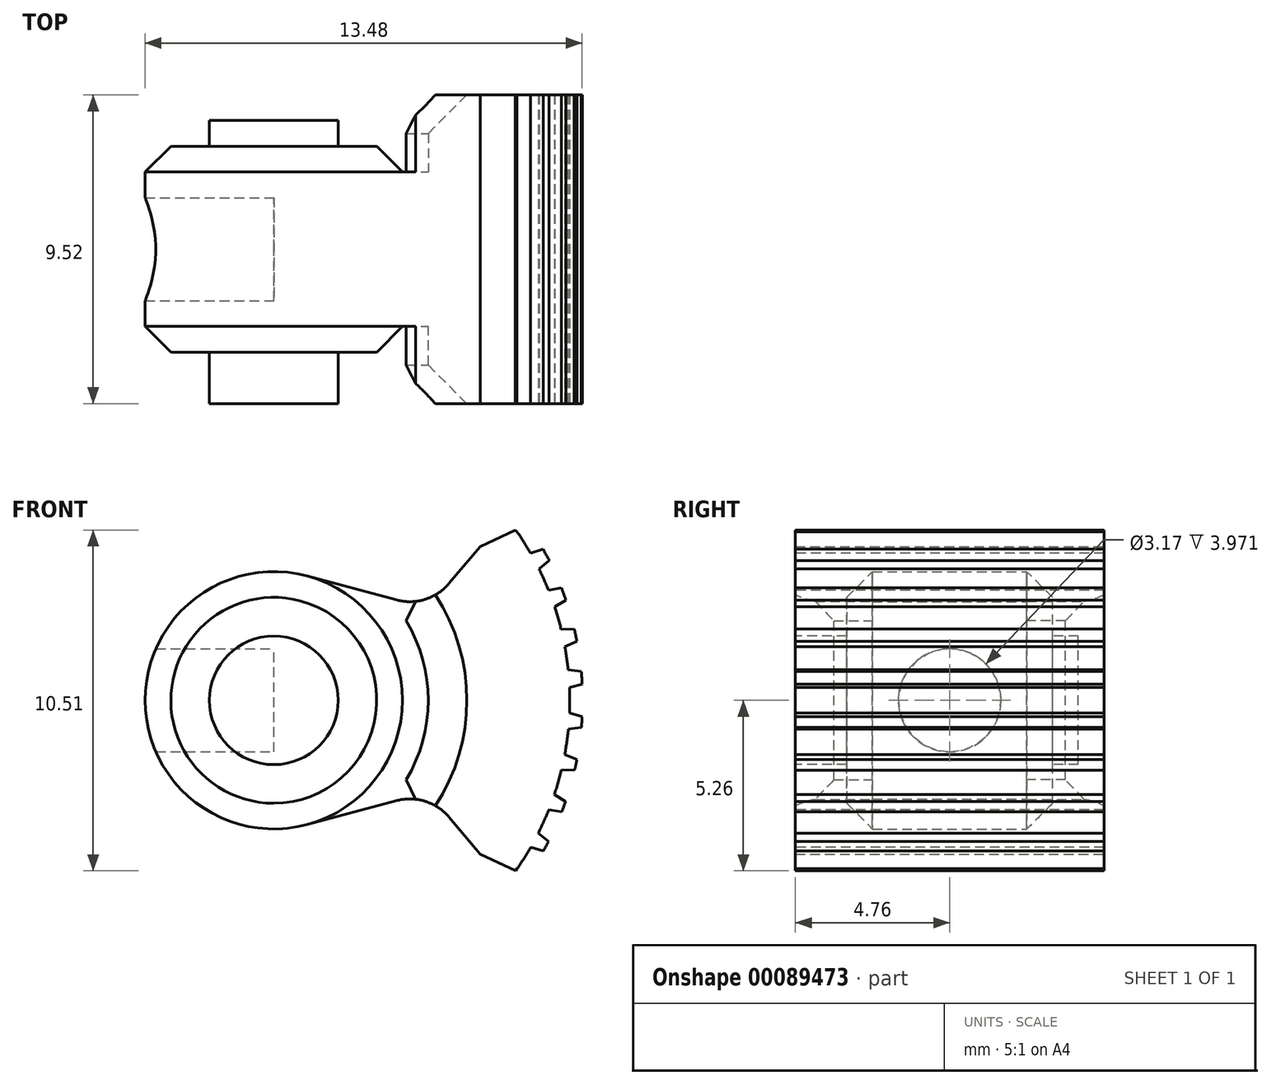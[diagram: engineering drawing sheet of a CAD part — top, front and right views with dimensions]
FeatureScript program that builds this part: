
annotation { "Feature Type Name" : "Feature", "Feature Type Description" : "" }
export const myFeature = defineFeature(function(context is Context, id is Id, definition is map)
    precondition{}
    {
        {
            var Q0;
            Q0=qCreatedBy(makeId("Front.planeOp"),FACE);
            var sketch = newSketch(context, id + "F0", { "sketchPlane" : qUnion([Q0])});
            skArc(sketch, "E0", {"start": v(7.83, -5.43) * mm, "mid": v(9.53, 0) * mm, "end": v(7.83, 5.43) * mm});
            skArc(sketch, "E1", {"start": v(6.36, -4.75) * mm, "mid": v(7.94, 0) * mm, "end": v(6.36, 4.75) * mm});
            skCircle(sketch, "E2", {"center": v(0, 0) * mm, "radius": 3.97 * mm});
            skLineSegment(sketch, "E3", {"start": v(1.03, 3.83) * mm, "end": v(3.78, 3.1) * mm});
            skLineSegment(sketch, "E4", {"start": v(5.4, 3.6) * mm, "end": v(6.36, 4.75) * mm});
            skLineSegment(sketch, "E5", {"start": v(6.36, 4.75) * mm, "end": v(7.83, 5.43) * mm});
            skLineSegment(sketch, "E6.MirrorCS", {"start": v(6.36, -4.75) * mm, "end": v(7.83, -5.43) * mm});
            skLineSegment(sketch, "E7.MirrorCS", {"start": v(1.03, -3.83) * mm, "end": v(3.78, -3.1) * mm});
            skLineSegment(sketch, "E8.MirrorCS", {"start": v(5.4, -3.6) * mm, "end": v(6.36, -4.75) * mm});
            skLineSegment(sketch, "E9", {"start": v(4.76, 2.83) * mm, "end": v(2.38, 0) * mm, "construction": true});
            skLineSegment(sketch, "E10", {"start": v(2.38, 0) * mm, "end": v(4.76, -2.83) * mm, "construction": true});
            skPoint(sketch, "E11.visualSharp", {"position": v(4.76, 2.83) * mm});
            skArc(sketch, "E11.filletArc", {"start": v(3.78, 3.1) * mm, "mid": v(4.67, 3.11) * mm, "end": v(5.4, 3.6) * mm});
            skPoint(sketch, "E12.visualSharp", {"position": v(4.76, -2.83) * mm});
            skArc(sketch, "E12.filletArc", {"start": v(5.4, -3.6) * mm, "mid": v(4.67, -3.11) * mm, "end": v(3.78, -3.1) * mm});
            skSolve(sketch);
        }
        {
            var Q0;
            {var subQ0=sQuery(id+"F0.wireOp",EDGE,"E2");var subQ1=makeQuery(id+"F0.imprint","INTERSECT",VERTEX,{"derivedFrom":[subQ0,sQuery(id+"F0.wireOp",EDGE,"E3")]});Q0=makeQuery(id+"F0.imprint","IMPRINT",FACE,{"disambiguationData":[TD([[makeQuery(id+"F0.imprint","IMPRINT",EDGE,{"disambiguationData":[TD([[subQ1,-1.0]])],"derivedFrom":subQ0}),1.0]])]});}
            var Q1;
            Q1=makeQuery(id+"F0.imprint","IMPRINT",FACE,{"disambiguationData":[TD([[makeQuery(id+"F0.imprint","IMPRINT",EDGE,{"derivedFrom":sQuery(id+"F0.wireOp",EDGE,"E1")}),1.0]])]});
            var Q2;
            Q2=makeQuery(id+"F0.imprint","IMPRINT",FACE,{"disambiguationData":[TD([[makeQuery(id+"F0.imprint","IMPRINT",EDGE,{"derivedFrom":sQuery(id+"F0.wireOp",EDGE,"E0")}),1.0]])]});
            extrude(context, id + "F1", {"entities" : qUnion([Q0, Q1, Q2]), "endBound" : BoundingType.SYMMETRIC, "depth" : 9.52 * mm});
        }
        {
            var Q0;
            Q0=qCreatedBy(makeId("Front.planeOp"),FACE);
            var sketch = newSketch(context, id + "F2", { "sketchPlane" : qUnion([Q0])});
            skCircle(sketch, "E13", {"center": v(0, 0) * mm, "radius": 4.76 * mm});
            skSolve(sketch);
        }
        {
            var Q0;
            Q0=makeQuery(id+"F2.imprint","IMPRINT",FACE,{"disambiguationData":[TD([[makeQuery(id+"F2.imprint","IMPRINT",EDGE,{"derivedFrom":sQuery(id+"F2.wireOp",EDGE,"E13")}),1.0]])]});
            extrude(context, id + "F3", {"entities" : qUnion([Q0]), "operationType" : NewBodyOperationType.REMOVE, "depth" : 25.4 * mm, "hasSecondDirection" : true, "secondDirectionOppositeDirection" : false, "secondDirectionDepth" : 2.38 * mm});
        }
        {
            var Q0;
            Q0=makeQuery(id+"F2.imprint","IMPRINT",FACE,{"disambiguationData":[TD([[makeQuery(id+"F2.imprint","IMPRINT",EDGE,{"derivedFrom":sQuery(id+"F2.wireOp",EDGE,"E13")}),1.0]])]});
            extrude(context, id + "F4", {"entities" : qUnion([Q0]), "operationType" : NewBodyOperationType.REMOVE, "oppositeDirection" : true, "depth" : 25.4 * mm, "hasSecondDirection" : true, "secondDirectionOppositeDirection" : true, "secondDirectionDepth" : 2.38 * mm});
        }
        {
            var Q0;
            Q0=qCreatedBy(makeId("Front.planeOp"),FACE);
            var sketch = newSketch(context, id + "F5", { "sketchPlane" : qUnion([Q0])});
            skCircle(sketch, "E14", {"center": v(0, 0) * mm, "radius": 1.98 * mm});
            skCircle(sketch, "E15", {"center": v(0, 0) * mm, "radius": 3.57 * mm});
            skSolve(sketch);
        }
        {
            var Q0;
            Q0=makeQuery(id+"F5.imprint","IMPRINT",FACE,{"disambiguationData":[TD([[makeQuery(id+"F5.imprint","IMPRINT",EDGE,{"derivedFrom":sQuery(id+"F5.wireOp",EDGE,"E14")}),1.0]])]});
            var Q1;
            Q1=makeQuery(id+"F5.imprint","IMPRINT",FACE,{"disambiguationData":[TD([[makeQuery(id+"F5.imprint","IMPRINT",EDGE,{"derivedFrom":sQuery(id+"F5.wireOp",EDGE,"E14")}),-1.0]])]});
            extrude(context, id + "F6", {"entities" : qUnion([Q0, Q1]), "endBound" : BoundingType.SYMMETRIC, "depth" : 6.35 * mm});
        }
        {
            var Q0;
            Q0=makeQuery(id+"F5.imprint","IMPRINT",FACE,{"disambiguationData":[TD([[makeQuery(id+"F5.imprint","IMPRINT",EDGE,{"derivedFrom":sQuery(id+"F5.wireOp",EDGE,"E14")}),1.0]])]});
            extrude(context, id + "F7", {"entities" : qUnion([Q0]), "operationType" : NewBodyOperationType.ADD, "oppositeDirection" : true, "depth" : 3.97 * mm, "hasSecondDirection" : true, "secondDirectionOppositeDirection" : false, "secondDirectionDepth" : 4.76 * mm});
        }
        {
            var Q0;
            Q0=makeQuery(id+"F6.opExtrude","SWEPT_FACE",FACE,{"disambiguationData":[OSD([sQuery(id+"F5.wireOp",EDGE,"E15")])]});
            chamfer(context, id + "F8", {"entities" : qUnion([Q0]), "width" : 0.4 * mm, "tangentPropagation" : true});
        }
        {
            var Q0;
            Q0=makeQuery(id+"F4.boolean.opBoolean","INTERSECT",EDGE,{"derivedFrom":[makeQuery(id+"F1.opExtrude","CAP_FACE",FACE,{"disambiguationData":[OSD([sQuery(id+"F0.wireOp",EDGE,"E0"),sQuery(id+"F0.wireOp",EDGE,"E2"),sQuery(id+"F0.wireOp",EDGE,"E3"),sQuery(id+"F0.wireOp",EDGE,"E4"),sQuery(id+"F0.wireOp",EDGE,"E5"),sQuery(id+"F0.wireOp",EDGE,"E6.MirrorCS"),sQuery(id+"F0.wireOp",EDGE,"E7.MirrorCS"),sQuery(id+"F0.wireOp",EDGE,"E8.MirrorCS"),sQuery(id+"F0.wireOp",EDGE,"E11.filletArc"),sQuery(id+"F0.wireOp",EDGE,"E12.filletArc")])],"isStart":true}),makeQuery(id+"F4.opExtrude","SWEPT_FACE",FACE,{"disambiguationData":[OSD([sQuery(id+"F2.wireOp",EDGE,"E13")])]})]});
            var Q1;
            Q1=makeQuery(id+"F3.boolean.opBoolean","INTERSECT",EDGE,{"derivedFrom":[makeQuery(id+"F1.opExtrude","CAP_FACE",FACE,{"disambiguationData":[OSD([sQuery(id+"F0.wireOp",EDGE,"E0"),sQuery(id+"F0.wireOp",EDGE,"E2"),sQuery(id+"F0.wireOp",EDGE,"E3"),sQuery(id+"F0.wireOp",EDGE,"E4"),sQuery(id+"F0.wireOp",EDGE,"E5"),sQuery(id+"F0.wireOp",EDGE,"E6.MirrorCS"),sQuery(id+"F0.wireOp",EDGE,"E7.MirrorCS"),sQuery(id+"F0.wireOp",EDGE,"E8.MirrorCS"),sQuery(id+"F0.wireOp",EDGE,"E11.filletArc"),sQuery(id+"F0.wireOp",EDGE,"E12.filletArc")])],"isStart":false}),makeQuery(id+"F3.opExtrude","SWEPT_FACE",FACE,{"disambiguationData":[OSD([sQuery(id+"F2.wireOp",EDGE,"E13")])]})]});
            chamfer(context, id + "F9", {"entities" : qUnion([Q0, Q1]), "width" : 1.2 * mm, "tangentPropagation" : true});
        }
        {
            var Q0;
            Q0=makeQuery(id+"F3.boolean.opBoolean","INTERSECT",EDGE,{"derivedFrom":[makeQuery(id+"F1.opExtrude","SWEPT_FACE",FACE,{"disambiguationData":[OSD([sQuery(id+"F0.wireOp",EDGE,"E3")])]}),makeQuery(id+"F3.opExtrude","SWEPT_FACE",FACE,{"disambiguationData":[OSD([sQuery(id+"F2.wireOp",EDGE,"E13")])]})]});
            var Q1;
            Q1=makeQuery(id+"F3.boolean.opBoolean","INTERSECT",EDGE,{"derivedFrom":[makeQuery(id+"F1.opExtrude","SWEPT_FACE",FACE,{"disambiguationData":[OSD([sQuery(id+"F0.wireOp",EDGE,"E7.MirrorCS")])]}),makeQuery(id+"F3.opExtrude","SWEPT_FACE",FACE,{"disambiguationData":[OSD([sQuery(id+"F2.wireOp",EDGE,"E13")])]})]});
            var Q2;
            Q2=makeQuery(id+"F4.boolean.opBoolean","INTERSECT",EDGE,{"derivedFrom":[makeQuery(id+"F1.opExtrude","SWEPT_FACE",FACE,{"disambiguationData":[OSD([sQuery(id+"F0.wireOp",EDGE,"E3")])]}),makeQuery(id+"F4.opExtrude","SWEPT_FACE",FACE,{"disambiguationData":[OSD([sQuery(id+"F2.wireOp",EDGE,"E13")])]})]});
            var Q3;
            Q3=makeQuery(id+"F4.boolean.opBoolean","INTERSECT",EDGE,{"derivedFrom":[makeQuery(id+"F1.opExtrude","SWEPT_FACE",FACE,{"disambiguationData":[OSD([sQuery(id+"F0.wireOp",EDGE,"E7.MirrorCS")])]}),makeQuery(id+"F4.opExtrude","SWEPT_FACE",FACE,{"disambiguationData":[OSD([sQuery(id+"F2.wireOp",EDGE,"E13")])]})]});
            chamfer(context, id + "F10", {"entities" : qUnion([Q0, Q1, Q2, Q3]), "width" : 0.4 * mm, "tangentPropagation" : true});
        }
        {
            var Q0;
            Q0=qCreatedBy(makeId("Right.planeOp"),FACE);
            var sketch = newSketch(context, id + "F11", { "sketchPlane" : qUnion([Q0])});
            skCircle(sketch, "E16", {"center": v(0, 0) * mm, "radius": 1.59 * mm});
            skSolve(sketch);
        }
        {
            var Q0;
            Q0 = qSketchRegion(id + "F11", true);
            var Q1;
            Q1 = qConstructionFilter(qBodyType(qCreatedBy(id + "F11" ,EDGE), BodyType.WIRE), ConstructionObject.NO);
            extrude(context, id + "F12", {"entities" : qUnion([Q0]), "operationType" : NewBodyOperationType.REMOVE, "surfaceEntities" : qUnion([Q1]), "oppositeDirection" : true, "depth" : 4.76 * mm});
        }
        {
            var Q0;
            Q0=qCreatedBy(makeId("Front.planeOp"),FACE);
            var sketch = newSketch(context, id + "F13", { "sketchPlane" : qUnion([Q0])});
            skArc(sketch, "E17.0", {"start": v(7.83, -5.43) * mm, "mid": v(9.53, 0) * mm, "end": v(7.83, 5.43) * mm});
            skArc(sketch, "E18.0", {"start": v(7.5, -5.2) * mm, "mid": v(7.72, -4.87) * mm, "end": v(7.93, -4.53) * mm});
            skLineSegment(sketch, "E19", {"start": v(9.08, 0.94) * mm, "end": v(9.48, 0.9) * mm});
            skLineSegment(sketch, "E20", {"start": v(9.51, 0.5) * mm, "end": v(9.12, 0.4) * mm});
            skLineSegment(sketch, "E21", {"start": v(9.12, -0.4) * mm, "end": v(9.51, -0.5) * mm});
            skLineSegment(sketch, "E22", {"start": v(9.12, 0.4) * mm, "end": v(9.12, -0.4) * mm, "construction": true});
            skLineSegment(sketch, "E23", {"start": v(0, 0) * mm, "end": v(9.12, 0) * mm, "construction": true});
            skLineSegment(sketch, "E24", {"start": v(0, 0) * mm, "end": v(9.08, 0.94) * mm, "construction": true});
            skLineSegment(sketch, "E25", {"start": v(0, 0) * mm, "end": v(9.12, -0.4) * mm, "construction": true});
            skLineSegment(sketch, "E26.1.0", {"start": v(9.49, -0.84) * mm, "end": v(9.09, -0.88) * mm});
            skLineSegment(sketch, "E26.1.1", {"start": v(9.09, -0.88) * mm, "end": v(8.97, -1.67) * mm, "construction": true});
            skLineSegment(sketch, "E26.1.2", {"start": v(8.97, -1.67) * mm, "end": v(9.35, -1.83) * mm});
            skLineSegment(sketch, "E26.2.0", {"start": v(9.28, -2.16) * mm, "end": v(8.87, -2.15) * mm});
            skLineSegment(sketch, "E26.2.1", {"start": v(8.87, -2.15) * mm, "end": v(8.65, -2.91) * mm, "construction": true});
            skLineSegment(sketch, "E26.2.2", {"start": v(8.65, -2.91) * mm, "end": v(9, -3.12) * mm});
            skLineSegment(sketch, "E26.3.0", {"start": v(8.88, -3.44) * mm, "end": v(8.48, -3.37) * mm});
            skLineSegment(sketch, "E26.3.1", {"start": v(8.48, -3.37) * mm, "end": v(8.16, -4.1) * mm, "construction": true});
            skLineSegment(sketch, "E26.3.2", {"start": v(8.16, -4.1) * mm, "end": v(8.47, -4.35) * mm});
            skLineSegment(sketch, "E26.4.0", {"start": v(8.32, -4.65) * mm, "end": v(7.93, -4.53) * mm});
            skLineSegment(sketch, "E26.4.1", {"start": v(7.93, -4.53) * mm, "end": v(7.5, -5.2) * mm, "construction": true});
            skLineSegment(sketch, "E26.anchor2", {"start": v(0, 0) * mm, "end": v(7.5, -5.2) * mm, "construction": true});
            skLineSegment(sketch, "E27.1.0", {"start": v(8.86, 2.2) * mm, "end": v(9.27, 2.2) * mm});
            skLineSegment(sketch, "E27.1.1", {"start": v(9.35, 1.81) * mm, "end": v(8.98, 1.66) * mm});
            skLineSegment(sketch, "E27.2.0", {"start": v(8.47, 3.4) * mm, "end": v(8.87, 3.46) * mm});
            skLineSegment(sketch, "E27.2.1", {"start": v(9, 3.1) * mm, "end": v(8.66, 2.88) * mm});
            skLineSegment(sketch, "E27.3.0", {"start": v(7.92, 4.54) * mm, "end": v(8.3, 4.66) * mm});
            skLineSegment(sketch, "E27.3.1", {"start": v(8.5, 4.3) * mm, "end": v(8.18, 4.05) * mm});
            skLineSegment(sketch, "E27.anchor2", {"start": v(0, 0) * mm, "end": v(7.92, 4.54) * mm, "construction": true});
            skArc(sketch, "E28", {"start": v(7.92, 4.54) * mm, "mid": v(7.72, 4.87) * mm, "end": v(7.5, 5.2) * mm});
            skArc(sketch, "E29", {"start": v(7.93, -4.53) * mm, "mid": v(9.13, 0) * mm, "end": v(7.92, 4.54) * mm});
            skLineSegment(sketch, "E30", {"start": v(7.83, 5.43) * mm, "end": v(6.32, 7.6) * mm});
            skLineSegment(sketch, "E31", {"start": v(6.32, 7.6) * mm, "end": v(5.48, 7) * mm});
            skLineSegment(sketch, "E32", {"start": v(5.48, 7) * mm, "end": v(7.5, 5.2) * mm});
            skLineSegment(sketch, "E33", {"start": v(7.83, -5.43) * mm, "end": v(6.96, -6.68) * mm});
            skLineSegment(sketch, "E34", {"start": v(6.96, -6.68) * mm, "end": v(6.6, -6.43) * mm});
            skLineSegment(sketch, "E35", {"start": v(6.6, -6.43) * mm, "end": v(7.5, -5.2) * mm});
            skSolve(sketch);
        }
        {
            var Q0;
            {var subQ1=sQuery(id+"F13.wireOp",EDGE,"E26.4.0");Q0=makeQuery(id+"F13.imprint","IMPRINT",FACE,{"disambiguationData":[TD([[makeQuery(id+"F13.imprint","IMPRINT",EDGE,{"derivedFrom":subQ1}),1.0]])]});}
            var Q1;
            {var subQ1=sQuery(id+"F13.wireOp",EDGE,"E27.3.0");Q1=makeQuery(id+"F13.imprint","IMPRINT",FACE,{"disambiguationData":[TD([[makeQuery(id+"F13.imprint","IMPRINT",EDGE,{"derivedFrom":subQ1}),1.0]])]});}
            var Q2;
            {var subQ0=sQuery(id+"F13.wireOp",EDGE,"E26.3.0");Q2=makeQuery(id+"F13.imprint","IMPRINT",FACE,{"disambiguationData":[TD([[makeQuery(id+"F13.imprint","IMPRINT",EDGE,{"derivedFrom":subQ0}),1.0]])]});}
            var Q3;
            {var subQ0=sQuery(id+"F13.wireOp",EDGE,"E26.2.0");Q3=makeQuery(id+"F13.imprint","IMPRINT",FACE,{"disambiguationData":[TD([[makeQuery(id+"F13.imprint","IMPRINT",EDGE,{"derivedFrom":subQ0}),1.0]])]});}
            var Q4;
            {var subQ0=sQuery(id+"F13.wireOp",EDGE,"E26.1.0");Q4=makeQuery(id+"F13.imprint","IMPRINT",FACE,{"disambiguationData":[TD([[makeQuery(id+"F13.imprint","IMPRINT",EDGE,{"derivedFrom":subQ0}),1.0]])]});}
            var Q5;
            {var subQ0=sQuery(id+"F13.wireOp",EDGE,"E20");Q5=makeQuery(id+"F13.imprint","IMPRINT",FACE,{"disambiguationData":[TD([[makeQuery(id+"F13.imprint","IMPRINT",EDGE,{"derivedFrom":subQ0}),1.0]])]});}
            var Q6;
            {var subQ0=sQuery(id+"F13.wireOp",EDGE,"E19");Q6=makeQuery(id+"F13.imprint","IMPRINT",FACE,{"disambiguationData":[TD([[makeQuery(id+"F13.imprint","IMPRINT",EDGE,{"derivedFrom":subQ0}),1.0]])]});}
            var Q7;
            {var subQ0=sQuery(id+"F13.wireOp",EDGE,"E27.1.0");Q7=makeQuery(id+"F13.imprint","IMPRINT",FACE,{"disambiguationData":[TD([[makeQuery(id+"F13.imprint","IMPRINT",EDGE,{"derivedFrom":subQ0}),1.0]])]});}
            var Q8;
            {var subQ0=sQuery(id+"F13.wireOp",EDGE,"E27.2.0");Q8=makeQuery(id+"F13.imprint","IMPRINT",FACE,{"disambiguationData":[TD([[makeQuery(id+"F13.imprint","IMPRINT",EDGE,{"derivedFrom":subQ0}),1.0]])]});}
            extrude(context, id + "F14", {"entities" : qUnion([Q0, Q1, Q2, Q3, Q4, Q5, Q6, Q7, Q8]), "operationType" : NewBodyOperationType.REMOVE, "endBound" : BoundingType.SYMMETRIC, "oppositeDirection" : true, "depth" : 12.7 * mm});
        }
    });
